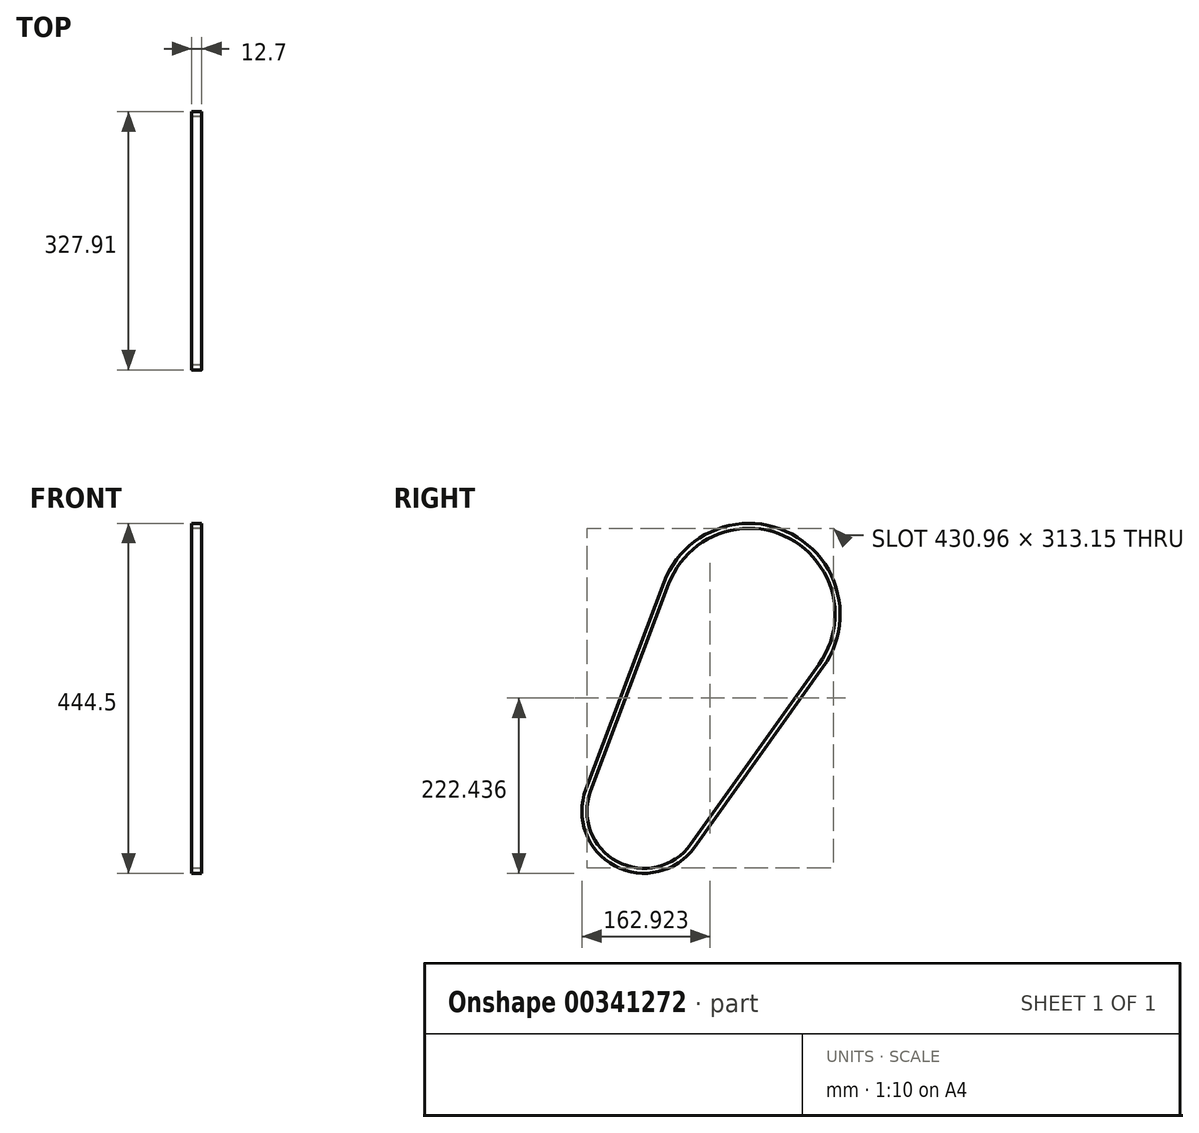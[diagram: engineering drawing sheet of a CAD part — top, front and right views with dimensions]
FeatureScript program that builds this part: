
annotation { "Feature Type Name" : "Feature", "Feature Type Description" : "" }
export const myFeature = defineFeature(function(context is Context, id is Id, definition is map)
    precondition{}
    {
        {
            var Q0;
            Q0=qCreatedBy(makeId("Right.planeOp"),FACE);
            var sketch = newSketch(context, id + "F0", { "sketchPlane" : qUnion([Q0])});
            skLineSegment(sketch, "E0", {"start": v(0, 0) * mm, "end": v(133.35, 0) * mm, "construction": true});
            skLineSegment(sketch, "E1", {"start": v(133.35, 0) * mm, "end": v(133.35, 249.94) * mm, "construction": true});
            skArc(sketch, "E2", {"start": v(-67.97, 25.63) * mm, "mid": v(-34.2, -64.1) * mm, "end": v(59.14, -42.18) * mm});
            skArc(sketch, "E3", {"start": v(222.27, 186.51) * mm, "mid": v(184.76, 346.3) * mm, "end": v(31.16, 288.48) * mm});
            skLineSegment(sketch, "E4", {"start": v(31.16, 288.48) * mm, "end": v(-67.97, 25.63) * mm});
            skLineSegment(sketch, "E5", {"start": v(222.27, 186.51) * mm, "end": v(59.14, -42.18) * mm});
            skLineSegment(sketch, "E6.0", {"start": v(25.21, 290.72) * mm, "end": v(-73.91, 27.87) * mm});
            skArc(sketch, "E6.1", {"start": v(227.44, 182.82) * mm, "mid": v(187.75, 351.9) * mm, "end": v(25.21, 290.72) * mm});
            skLineSegment(sketch, "E6.2", {"start": v(227.44, 182.82) * mm, "end": v(64.31, -45.87) * mm});
            skArc(sketch, "E6.3", {"start": v(-73.91, 27.87) * mm, "mid": v(-37.18, -69.7) * mm, "end": v(64.31, -45.87) * mm});
            skSolve(sketch);
        }
        {
            var Q0;
            Q0=qSketchRegion(id+"F0",true);
            extrude(context, id + "F1", {"entities" : qUnion([Q0]), "endBound" : BoundingType.SYMMETRIC, "depth" : 12.7 * mm});
        }
    });
